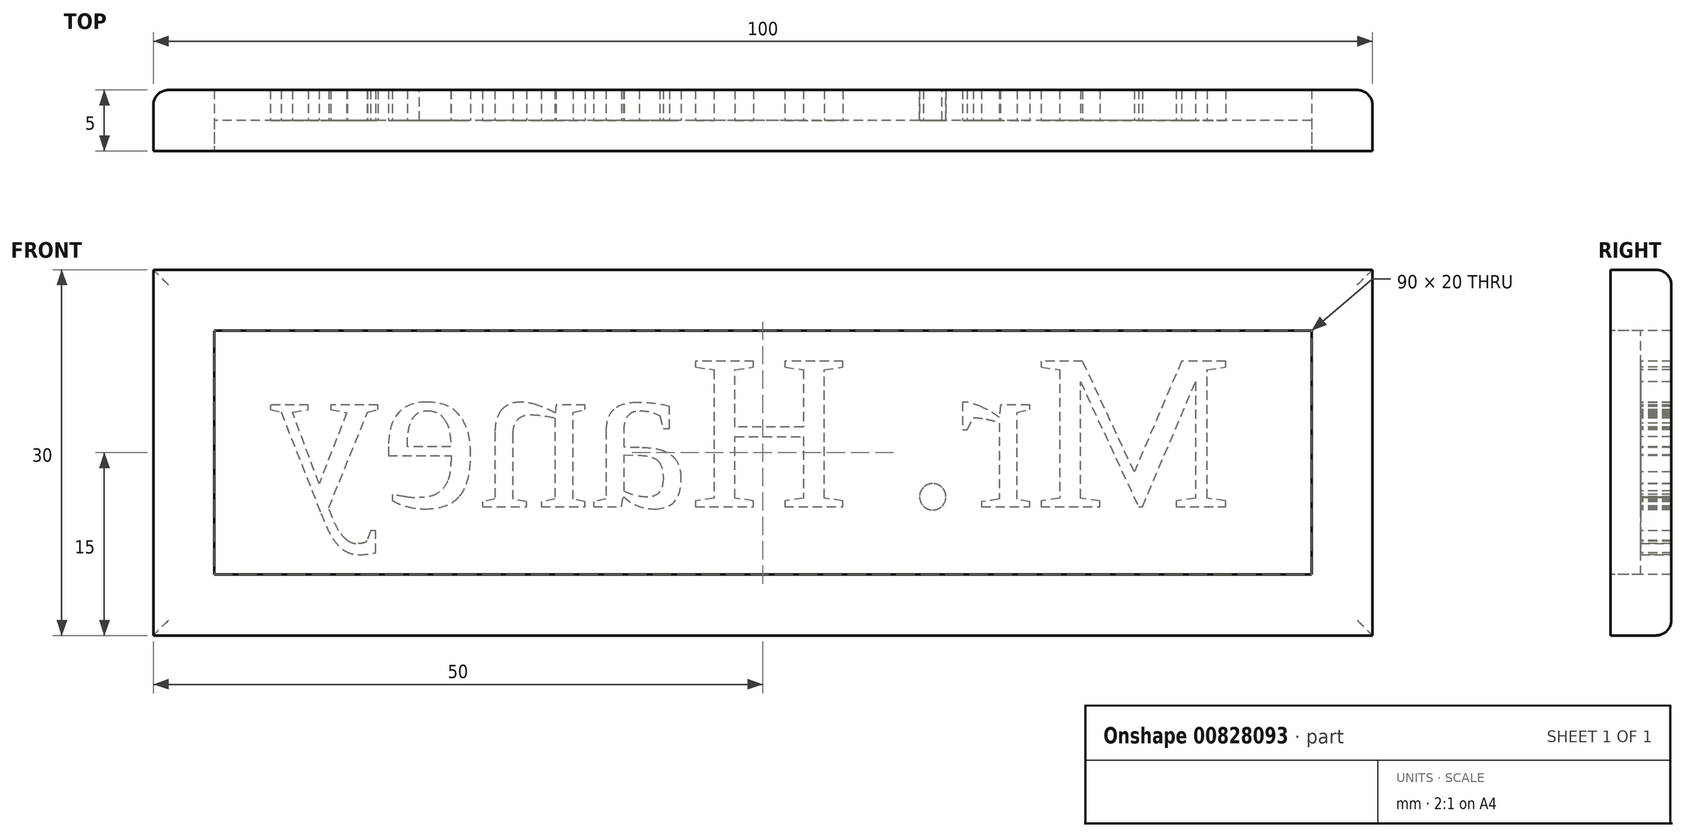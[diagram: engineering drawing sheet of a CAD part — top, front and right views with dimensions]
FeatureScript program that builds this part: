
annotation { "Feature Type Name" : "Feature", "Feature Type Description" : "" }
export const myFeature = defineFeature(function(context is Context, id is Id, definition is map)
    precondition{}
    {
        {
            var Q0;
            Q0=qCreatedBy(makeId("Front.planeOp"),FACE);
            var sketch = newSketch(context, id + "F0", { "sketchPlane" : qUnion([Q0])});
            skLineSegment(sketch, "E0.bottom", {"start": v(50, -15) * mm, "end": v(-50, -15) * mm});
            skLineSegment(sketch, "E0.top", {"start": v(50, 15) * mm, "end": v(-50, 15) * mm});
            skLineSegment(sketch, "E0.left", {"start": v(50, -15) * mm, "end": v(50, 15) * mm});
            skLineSegment(sketch, "E0.right", {"start": v(-50, -15) * mm, "end": v(-50, 15) * mm});
            skPoint(sketch, "E0.middle", {"position": v(0, 0) * mm});
            skLineSegment(sketch, "E1.bottom", {"start": v(45, -10) * mm, "end": v(-45, -10) * mm});
            skLineSegment(sketch, "E1.top", {"start": v(45, 10) * mm, "end": v(-45, 10) * mm});
            skLineSegment(sketch, "E1.left", {"start": v(45, -10) * mm, "end": v(45, 10) * mm});
            skLineSegment(sketch, "E1.right", {"start": v(-45, -10) * mm, "end": v(-45, 10) * mm});
            skSolve(sketch);
        }
        {
            var Q0;
            Q0=makeQuery(id+"F0.imprint","IMPRINT",FACE,{"disambiguationData":[TD([[makeQuery(id+"F0.imprint","IMPRINT",EDGE,{"derivedFrom":sQuery(id+"F0.wireOp",EDGE,"E0.bottom")}),-1.0]])]});
            extrude(context, id + "F1", {"entities" : qUnion([Q0]), "oppositeDirection" : true, "depth" : 5 * mm, "offsetDistance" : 25 * mm});
        }
        {
            var Q0;
            Q0=makeQuery(id+"F0.imprint","IMPRINT",FACE,{"disambiguationData":[TD([[makeQuery(id+"F0.imprint","IMPRINT",EDGE,{"derivedFrom":sQuery(id+"F0.wireOp",EDGE,"E1.bottom")}),-1.0]])]});
            extrude(context, id + "F2", {"entities" : qUnion([Q0]), "oppositeDirection" : true, "depth" : 2.5 * mm, "offsetDistance" : 25 * mm});
        }
        {
            var Q0;
            Q0=makeQuery(id+"F1.opExtrude","CAP_EDGE",EDGE,{"disambiguationData":[OSD([sQuery(id+"F0.wireOp",EDGE,"E0.top")])],"isStart":false});
            var Q1;
            Q1=makeQuery(id+"F1.opExtrude","CAP_EDGE",EDGE,{"disambiguationData":[OSD([sQuery(id+"F0.wireOp",EDGE,"E0.left")])],"isStart":false});
            var Q2;
            Q2=makeQuery(id+"F1.opExtrude","CAP_EDGE",EDGE,{"disambiguationData":[OSD([sQuery(id+"F0.wireOp",EDGE,"E0.bottom")])],"isStart":false});
            var Q3;
            Q3=makeQuery(id+"F1.opExtrude","CAP_EDGE",EDGE,{"disambiguationData":[OSD([sQuery(id+"F0.wireOp",EDGE,"E0.right")])],"isStart":false});
            fillet(context, id + "F3", {"entities" : qUnion([Q0, Q1, Q2, Q3]), "radius" : 1.25 * mm, "tangentPropagation" : true, "allowEdgeOverflow" : false});
        }
        {
            var Q0;
            Q0=makeQuery(id+"F2.opExtrude","CAP_FACE",FACE,{"disambiguationData":[OSD([sQuery(id+"F0.wireOp",EDGE,"E1.bottom"),sQuery(id+"F0.wireOp",EDGE,"E1.top"),sQuery(id+"F0.wireOp",EDGE,"E1.left"),sQuery(id+"F0.wireOp",EDGE,"E1.right")])],"isStart":false});
            var sketch = newSketch(context, id + "F4", { "sketchPlane" : qUnion([Q0])});
            skText(sketch, "E2", { "text": "Mr. Haney", "fontName": "Tinos-Regular.ttf"});
            const initialGuessF4  = {"E2": [-0.03848, -0.00444, 1, 0, 0.01312]};
            skSetInitialGuess(sketch, initialGuessF4);
            skSolve(sketch);
        }
        {
            var Q0;
            Q0 = qSketchRegion(id + "F4", true);
            extrude(context, id + "F5", {"entities" : qUnion([Q0]), "operationType" : NewBodyOperationType.ADD, "depth" : 2.5 * mm, "offsetDistance" : 25 * mm});
        }
    });
